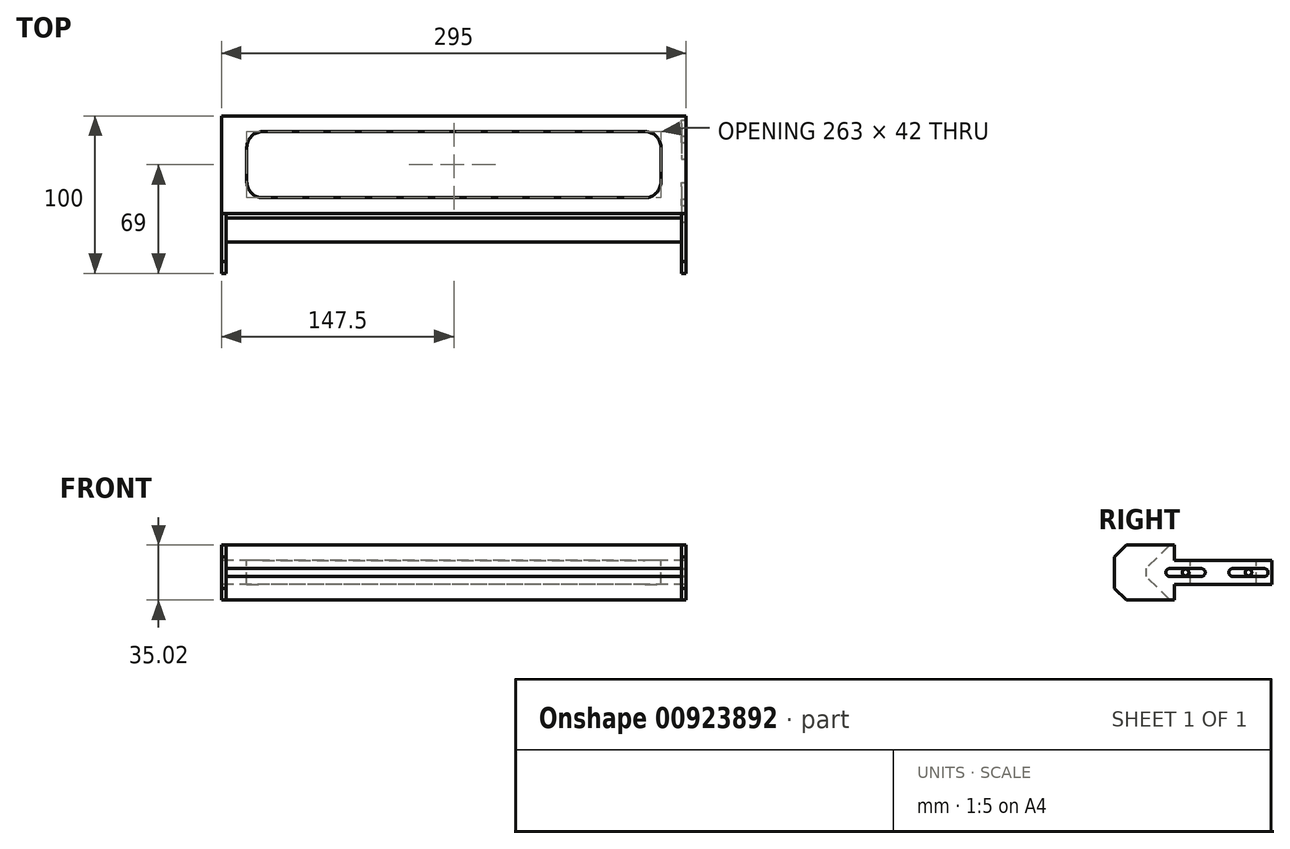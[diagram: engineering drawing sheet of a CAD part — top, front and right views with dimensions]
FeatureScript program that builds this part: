
annotation { "Feature Type Name" : "Feature", "Feature Type Description" : "" }
export const myFeature = defineFeature(function(context is Context, id is Id, definition is map)
    precondition{}
    {
        {
            var Q0;
            Q0=qCreatedBy(makeId("Top.planeOp"),FACE);
            var sketch = newSketch(context, id + "F0", { "sketchPlane" : qUnion([Q0])});
            skLineSegment(sketch, "E0.bottom", {"start": v(147.5, 50) * mm, "end": v(-147.5, 50) * mm});
            skLineSegment(sketch, "E0.top", {"start": v(147.5, -50) * mm, "end": v(144.5, -50) * mm});
            skLineSegment(sketch, "E0.left", {"start": v(147.5, 50) * mm, "end": v(147.5, -50) * mm});
            skLineSegment(sketch, "E0.right", {"start": v(-147.5, 50) * mm, "end": v(-147.5, -50) * mm});
            skPoint(sketch, "E0.middle", {"position": v(0, 0) * mm});
            skLineSegment(sketch, "E1", {"start": v(-144.5, -50) * mm, "end": v(-144.5, -30) * mm});
            skLineSegment(sketch, "E2", {"start": v(-144.5, -30) * mm, "end": v(144.5, -30) * mm});
            skLineSegment(sketch, "E3", {"start": v(144.5, -30) * mm, "end": v(144.5, -50) * mm});
            skLineSegment(sketch, "E4.trimOffspring", {"start": v(-144.5, -50) * mm, "end": v(-147.5, -50) * mm});
            skSolve(sketch);
        }
        {
            var Q0;
            Q0=qSketchRegion(id+"F0",true);
            extrude(context, id + "F1", {"entities" : qUnion([Q0]), "depth" : 17.5 * mm, "offsetDistance" : 25 * mm, "hasSecondDirection" : true, "secondDirectionOppositeDirection" : true, "secondDirectionDepth" : 17.5 * mm});
        }
        {
            var Q0;
            Q0=makeQuery(id+"F1.opExtrude","CAP_EDGE",EDGE,{"disambiguationData":[OSD([sQuery(id+"F0.wireOp",EDGE,"E2")])],"isStart":false});
            var Q1;
            Q1=makeQuery(id+"F1.opExtrude","CAP_EDGE",EDGE,{"disambiguationData":[OSD([sQuery(id+"F0.wireOp",EDGE,"E2")])],"isStart":true});
            chamfer(context, id + "F2", {"entities" : qUnion([Q0, Q1]), "width" : 15 * mm, "tangentPropagation" : true});
        }
        {
            var Q0;
            Q0=makeQuery(id+"F1.opExtrude","CAP_EDGE",EDGE,{"disambiguationData":[OSD([sQuery(id+"F0.wireOp",EDGE,"E0.top")])],"isStart":false});
            var Q1;
            Q1=makeQuery(id+"F1.opExtrude","CAP_EDGE",EDGE,{"disambiguationData":[OSD([sQuery(id+"F0.wireOp",EDGE,"E0.top")])],"isStart":true});
            var Q2;
            Q2=makeQuery(id+"F1.opExtrude","CAP_EDGE",EDGE,{"disambiguationData":[OSD([sQuery(id+"F0.wireOp",EDGE,"E4.trimOffspring")])],"isStart":false});
            var Q3;
            Q3=makeQuery(id+"F1.opExtrude","CAP_EDGE",EDGE,{"disambiguationData":[OSD([sQuery(id+"F0.wireOp",EDGE,"E4.trimOffspring")])],"isStart":true});
            chamfer(context, id + "F3", {"entities" : qUnion([Q0, Q1, Q2, Q3]), "width" : 7.5 * mm, "tangentPropagation" : true});
        }
        {
            var Q0;
            Q0=makeQuery(id+"F1.opExtrude","SWEPT_FACE",FACE,{"disambiguationData":[OSD([sQuery(id+"F0.wireOp",EDGE,"E0.left")])]});
            var sketch = newSketch(context, id + "F4", { "sketchPlane" : qUnion([Q0])});
            skLineSegment(sketch, "E5.bottom", {"start": v(45, 2.5) * mm, "end": v(25, 2.5) * mm});
            skLineSegment(sketch, "E5.top", {"start": v(45, -2.5) * mm, "end": v(25, -2.5) * mm});
            skLineSegment(sketch, "E5.left", {"start": v(47.5, 0) * mm, "end": v(47.5, 0) * mm});
            skLineSegment(sketch, "E5.right", {"start": v(22.5, 0) * mm, "end": v(22.5, 0) * mm});
            skLineSegment(sketch, "E6.bottom", {"start": v(5, 2.5) * mm, "end": v(-15, 2.5) * mm});
            skLineSegment(sketch, "E6.top", {"start": v(5, -2.5) * mm, "end": v(-15, -2.5) * mm});
            skLineSegment(sketch, "E6.left", {"start": v(7.5, 0) * mm, "end": v(7.5, 0) * mm});
            skLineSegment(sketch, "E6.right", {"start": v(-17.5, 0) * mm, "end": v(-17.5, 0) * mm});
            skPoint(sketch, "E7.visualSharp", {"position": v(-17.5, 2.5) * mm});
            skArc(sketch, "E7.filletArc", {"start": v(-15, 2.5) * mm, "mid": v(-16.77, 1.77) * mm, "end": v(-17.5, 0) * mm});
            skPoint(sketch, "E8.visualSharp", {"position": v(-17.5, -2.5) * mm});
            skArc(sketch, "E8.filletArc", {"start": v(-17.5, 0) * mm, "mid": v(-16.77, -1.77) * mm, "end": v(-15, -2.5) * mm});
            skPoint(sketch, "E9.visualSharp", {"position": v(7.5, 2.5) * mm});
            skArc(sketch, "E9.filletArc", {"start": v(7.5, 0) * mm, "mid": v(6.77, 1.77) * mm, "end": v(5, 2.5) * mm});
            skPoint(sketch, "E10.visualSharp", {"position": v(7.5, -2.5) * mm});
            skArc(sketch, "E10.filletArc", {"start": v(5, -2.5) * mm, "mid": v(6.77, -1.77) * mm, "end": v(7.5, 0) * mm});
            skPoint(sketch, "E11.visualSharp", {"position": v(22.5, 2.5) * mm});
            skArc(sketch, "E11.filletArc", {"start": v(25, 2.5) * mm, "mid": v(23.23, 1.77) * mm, "end": v(22.5, 0) * mm});
            skPoint(sketch, "E12.visualSharp", {"position": v(22.5, -2.5) * mm});
            skArc(sketch, "E12.filletArc", {"start": v(22.5, 0) * mm, "mid": v(23.23, -1.77) * mm, "end": v(25, -2.5) * mm});
            skPoint(sketch, "E13.visualSharp", {"position": v(47.5, 2.5) * mm});
            skArc(sketch, "E13.filletArc", {"start": v(47.5, 0) * mm, "mid": v(46.77, 1.77) * mm, "end": v(45, 2.5) * mm});
            skPoint(sketch, "E14.visualSharp", {"position": v(47.5, -2.5) * mm});
            skArc(sketch, "E14.filletArc", {"start": v(45, -2.5) * mm, "mid": v(46.77, -1.77) * mm, "end": v(47.5, 0) * mm});
            skCircle(sketch, "E15", {"center": v(-5, 0) * mm, "radius": 2.1 * mm});
            skCircle(sketch, "E16", {"center": v(35, 0) * mm, "radius": 2.1 * mm});
            skPoint(sketch, "E16.centerSnap0", {"position": v(35, -2.5) * mm});
            skLineSegment(sketch, "E17", {"start": v(-50, 0) * mm, "end": v(50, 0) * mm, "construction": true});
            skSolve(sketch);
        }
        {
            var Q0;
            Q0=makeQuery(id+"F1.opExtrude","CAP_FACE",FACE,{"disambiguationData":[OSD([sQuery(id+"F0.wireOp",EDGE,"E0.bottom"),sQuery(id+"F0.wireOp",EDGE,"E0.top"),sQuery(id+"F0.wireOp",EDGE,"E0.left"),sQuery(id+"F0.wireOp",EDGE,"E0.right"),sQuery(id+"F0.wireOp",EDGE,"E1"),sQuery(id+"F0.wireOp",EDGE,"E2"),sQuery(id+"F0.wireOp",EDGE,"E3"),sQuery(id+"F0.wireOp",EDGE,"E4.trimOffspring")])],"isStart":false});
            var sketch = newSketch(context, id + "F5", { "sketchPlane" : qUnion([Q0])});
            skLineSegment(sketch, "E18.bottom", {"start": v(-147.5, 50) * mm, "end": v(-144.5, 50) * mm});
            skLineSegment(sketch, "E18.top", {"start": v(-147.5, -42.5) * mm, "end": v(-144.5, -42.5) * mm});
            skLineSegment(sketch, "E18.left", {"start": v(-147.5, 50) * mm, "end": v(-147.5, -42.5) * mm});
            skLineSegment(sketch, "E18.right", {"start": v(-144.5, 50) * mm, "end": v(-144.5, -42.5) * mm});
            skLineSegment(sketch, "E19.bottom", {"start": v(147.5, 50) * mm, "end": v(144.5, 50) * mm});
            skLineSegment(sketch, "E19.top", {"start": v(147.5, -42.5) * mm, "end": v(144.5, -42.5) * mm});
            skLineSegment(sketch, "E19.left", {"start": v(147.5, 50) * mm, "end": v(147.5, -42.5) * mm});
            skLineSegment(sketch, "E19.right", {"start": v(144.5, 50) * mm, "end": v(144.5, -42.5) * mm});
            skSolve(sketch);
        }
        {
            var Q0;
            Q0=qSketchRegion(id+"F5",true);
            extrude(context, id + "F6", {"entities" : qUnion([Q0]), "operationType" : NewBodyOperationType.ADD, "depth" : 0.01 * mm, "offsetDistance" : 25 * mm});
        }
        {
            var Q0;
            Q0=makeQuery(id+"F1.opExtrude","CAP_FACE",FACE,{"disambiguationData":[OSD([sQuery(id+"F0.wireOp",EDGE,"E0.bottom"),sQuery(id+"F0.wireOp",EDGE,"E0.top"),sQuery(id+"F0.wireOp",EDGE,"E0.left"),sQuery(id+"F0.wireOp",EDGE,"E0.right"),sQuery(id+"F0.wireOp",EDGE,"E1"),sQuery(id+"F0.wireOp",EDGE,"E2"),sQuery(id+"F0.wireOp",EDGE,"E3"),sQuery(id+"F0.wireOp",EDGE,"E4.trimOffspring")])],"isStart":true});
            var sketch = newSketch(context, id + "F7", { "sketchPlane" : qUnion([Q0])});
            skLineSegment(sketch, "E20.bottom", {"start": v(-147.5, -50) * mm, "end": v(-144.5, -50) * mm});
            skLineSegment(sketch, "E20.top", {"start": v(-147.5, 42.5) * mm, "end": v(-144.5, 42.5) * mm});
            skLineSegment(sketch, "E20.left", {"start": v(-147.5, -50) * mm, "end": v(-147.5, 42.5) * mm});
            skLineSegment(sketch, "E20.right", {"start": v(-144.5, -50) * mm, "end": v(-144.5, 42.5) * mm});
            skLineSegment(sketch, "E21.bottom", {"start": v(147.5, -50) * mm, "end": v(144.5, -50) * mm});
            skLineSegment(sketch, "E21.top", {"start": v(147.5, 42.5) * mm, "end": v(144.5, 42.5) * mm});
            skLineSegment(sketch, "E21.left", {"start": v(147.5, -50) * mm, "end": v(147.5, 42.5) * mm});
            skLineSegment(sketch, "E21.right", {"start": v(144.5, -50) * mm, "end": v(144.5, 42.5) * mm});
            skSolve(sketch);
        }
        {
            var Q0;
            Q0=qSketchRegion(id+"F7",true);
            extrude(context, id + "F8", {"entities" : qUnion([Q0]), "operationType" : NewBodyOperationType.ADD, "depth" : 0.01 * mm, "offsetDistance" : 25 * mm});
        }
        {
            var Q0;
            Q0=makeQuery(id+"F4.imprint","IMPRINT",FACE,{"disambiguationData":[TD([[makeQuery(id+"F4.imprint","IMPRINT",EDGE,{"derivedFrom":sQuery(id+"F4.wireOp",EDGE,"E5.bottom")}),1.0]])]});
            var Q1;
            Q1=makeQuery(id+"F4.imprint","IMPRINT",FACE,{"disambiguationData":[TD([[makeQuery(id+"F4.imprint","IMPRINT",EDGE,{"derivedFrom":sQuery(id+"F4.wireOp",EDGE,"E6.bottom")}),1.0]])]});
            extrude(context, id + "F9", {"entities" : qUnion([Q0, Q1]), "operationType" : NewBodyOperationType.REMOVE, "oppositeDirection" : true, "depth" : 3 * mm, "offsetDistance" : 25 * mm});
        }
        {
            var Q0;
            Q0=makeQuery(id+"F1.opExtrude","CAP_FACE",FACE,{"disambiguationData":[OSD([sQuery(id+"F0.wireOp",EDGE,"E0.bottom"),sQuery(id+"F0.wireOp",EDGE,"E0.top"),sQuery(id+"F0.wireOp",EDGE,"E0.left"),sQuery(id+"F0.wireOp",EDGE,"E0.right"),sQuery(id+"F0.wireOp",EDGE,"E1"),sQuery(id+"F0.wireOp",EDGE,"E2"),sQuery(id+"F0.wireOp",EDGE,"E3"),sQuery(id+"F0.wireOp",EDGE,"E4.trimOffspring")])],"isStart":false});
            var sketch = newSketch(context, id + "F10", { "sketchPlane" : qUnion([Q0])});
            skLineSegment(sketch, "E22.bottom", {"start": v(-141.5, 50) * mm, "end": v(141.5, 50) * mm});
            skLineSegment(sketch, "E22.top", {"start": v(-131.5, -12) * mm, "end": v(131.5, -12) * mm});
            skLineSegment(sketch, "E22.left", {"start": v(-141.5, 50) * mm, "end": v(-141.5, -2) * mm});
            skLineSegment(sketch, "E22.right", {"start": v(141.5, 50) * mm, "end": v(141.5, -2) * mm});
            skPoint(sketch, "E23.visualSharp", {"position": v(-141.5, -12) * mm});
            skArc(sketch, "E23.filletArc", {"start": v(-141.5, -2) * mm, "mid": v(-138.57, -9.07) * mm, "end": v(-131.5, -12) * mm});
            skPoint(sketch, "E24.visualSharp", {"position": v(141.5, -12) * mm});
            skArc(sketch, "E24.filletArc", {"start": v(131.5, -12) * mm, "mid": v(138.57, -9.07) * mm, "end": v(141.5, -2) * mm});
            skSolve(sketch);
        }
        {
            var Q0;
            Q0=makeQuery(id+"F10.imprint","IMPRINT",FACE,{"disambiguationData":[TD([[makeQuery(id+"F10.imprint","IMPRINT",EDGE,{"derivedFrom":sQuery(id+"F10.wireOp",EDGE,"E22.bottom")}),1.0]])]});
            extrude(context, id + "F11", {"entities" : qUnion([Q0]), "operationType" : NewBodyOperationType.REMOVE, "oppositeDirection" : true, "depth" : 10 * mm, "offsetDistance" : 25 * mm});
        }
        {
            var Q0;
            Q0=makeQuery(id+"F1.opExtrude","CAP_FACE",FACE,{"disambiguationData":[OSD([sQuery(id+"F0.wireOp",EDGE,"E0.bottom"),sQuery(id+"F0.wireOp",EDGE,"E0.top"),sQuery(id+"F0.wireOp",EDGE,"E0.left"),sQuery(id+"F0.wireOp",EDGE,"E0.right"),sQuery(id+"F0.wireOp",EDGE,"E1"),sQuery(id+"F0.wireOp",EDGE,"E2"),sQuery(id+"F0.wireOp",EDGE,"E3"),sQuery(id+"F0.wireOp",EDGE,"E4.trimOffspring")])],"isStart":true});
            var sketch = newSketch(context, id + "F12", { "sketchPlane" : qUnion([Q0])});
            skLineSegment(sketch, "E25.0.0", {"start": v(141.5, 2) * mm, "end": v(141.5, -50) * mm});
            skLineSegment(sketch, "E25.0.1", {"start": v(141.5, -50) * mm, "end": v(-141.5, -50) * mm});
            skLineSegment(sketch, "E25.0.2", {"start": v(-141.5, -50) * mm, "end": v(-141.5, 2) * mm});
            skArc(sketch, "E25.0.3", {"start": v(-141.5, 2) * mm, "mid": v(-138.57, 9.07) * mm, "end": v(-131.5, 12) * mm});
            skLineSegment(sketch, "E25.0.4", {"start": v(-131.5, 12) * mm, "end": v(131.5, 12) * mm});
            skArc(sketch, "E25.0.5", {"start": v(131.5, 12) * mm, "mid": v(138.57, 9.07) * mm, "end": v(141.5, 2) * mm});
            skSolve(sketch);
        }
        {
            var Q0;
            Q0=qSketchRegion(id+"F12",true);
            extrude(context, id + "F13", {"entities" : qUnion([Q0]), "operationType" : NewBodyOperationType.REMOVE, "oppositeDirection" : true, "depth" : 10 * mm, "offsetDistance" : 25 * mm});
        }
        {
            var Q0;
            Q0=makeQuery(id+"F11.boolean.opBoolean","COPY",FACE,{"derivedFrom":makeQuery(id+"F11.opExtrude","CAP_FACE",FACE,{"disambiguationData":[OSD([sQuery(id+"F10.wireOp",EDGE,"E22.bottom"),sQuery(id+"F10.wireOp",EDGE,"E22.top"),sQuery(id+"F10.wireOp",EDGE,"E22.left"),sQuery(id+"F10.wireOp",EDGE,"E22.right"),sQuery(id+"F10.wireOp",EDGE,"E23.filletArc"),sQuery(id+"F10.wireOp",EDGE,"E24.filletArc")])],"isStart":false})});
            var sketch = newSketch(context, id + "F14", { "sketchPlane" : qUnion([Q0])});
            skLineSegment(sketch, "E26.bottom", {"start": v(-121.5, 40) * mm, "end": v(121.5, 40) * mm});
            skLineSegment(sketch, "E26.top", {"start": v(-121.5, -2) * mm, "end": v(121.5, -2) * mm});
            skLineSegment(sketch, "E26.left", {"start": v(-131.5, 30) * mm, "end": v(-131.5, 8) * mm});
            skLineSegment(sketch, "E26.right", {"start": v(131.5, 30) * mm, "end": v(131.5, 8) * mm});
            skPoint(sketch, "E27.visualSharp", {"position": v(-131.5, 40) * mm});
            skArc(sketch, "E27.filletArc", {"start": v(-121.5, 40) * mm, "mid": v(-128.57, 37.07) * mm, "end": v(-131.5, 30) * mm});
            skPoint(sketch, "E28.visualSharp", {"position": v(-131.5, -2) * mm});
            skArc(sketch, "E28.filletArc", {"start": v(-131.5, 8) * mm, "mid": v(-128.57, 0.93) * mm, "end": v(-121.5, -2) * mm});
            skPoint(sketch, "E29.visualSharp", {"position": v(131.5, 40) * mm});
            skArc(sketch, "E29.filletArc", {"start": v(131.5, 30) * mm, "mid": v(128.57, 37.07) * mm, "end": v(121.5, 40) * mm});
            skPoint(sketch, "E30.visualSharp", {"position": v(131.5, -2) * mm});
            skArc(sketch, "E30.filletArc", {"start": v(121.5, -2) * mm, "mid": v(128.57, 0.93) * mm, "end": v(131.5, 8) * mm});
            skSolve(sketch);
        }
        {
            var Q0;
            Q0=makeQuery(id+"F14.imprint","IMPRINT",FACE,{"disambiguationData":[TD([[makeQuery(id+"F14.imprint","IMPRINT",EDGE,{"derivedFrom":sQuery(id+"F14.wireOp",EDGE,"E26.bottom")}),-1.0]])]});
            extrude(context, id + "F15", {"entities" : qUnion([Q0]), "operationType" : NewBodyOperationType.REMOVE, "oppositeDirection" : true, "depth" : 25 * mm, "offsetDistance" : 25 * mm});
        }
        {
            var Q0;
            Q0=makeQuery(id+"F1.opExtrude","CAP_FACE",FACE,{"disambiguationData":[OSD([sQuery(id+"F0.wireOp",EDGE,"E0.bottom"),sQuery(id+"F0.wireOp",EDGE,"E0.top"),sQuery(id+"F0.wireOp",EDGE,"E0.left"),sQuery(id+"F0.wireOp",EDGE,"E0.right"),sQuery(id+"F0.wireOp",EDGE,"E1"),sQuery(id+"F0.wireOp",EDGE,"E2"),sQuery(id+"F0.wireOp",EDGE,"E3"),sQuery(id+"F0.wireOp",EDGE,"E4.trimOffspring")])],"isStart":false});
            var sketch = newSketch(context, id + "F16", { "sketchPlane" : qUnion([Q0])});
            skLineSegment(sketch, "E31.bottom", {"start": v(-147.5, 50) * mm, "end": v(147.5, 50) * mm});
            skLineSegment(sketch, "E31.top", {"start": v(-147.5, -12) * mm, "end": v(147.5, -12) * mm});
            skLineSegment(sketch, "E31.left", {"start": v(-147.5, 50) * mm, "end": v(-147.5, -12) * mm});
            skLineSegment(sketch, "E31.right", {"start": v(147.5, 50) * mm, "end": v(147.5, -12) * mm});
            skSolve(sketch);
        }
        {
            var Q0;
            Q0 = qSketchRegion(id + "F16", true);
            var Q1;
            Q1=makeQuery(id+"F11.boolean.opBoolean","COPY",FACE,{"derivedFrom":makeQuery(id+"F11.opExtrude","CAP_FACE",FACE,{"disambiguationData":[OSD([sQuery(id+"F10.wireOp",EDGE,"E22.bottom"),sQuery(id+"F10.wireOp",EDGE,"E22.top"),sQuery(id+"F10.wireOp",EDGE,"E22.left"),sQuery(id+"F10.wireOp",EDGE,"E22.right"),sQuery(id+"F10.wireOp",EDGE,"E23.filletArc"),sQuery(id+"F10.wireOp",EDGE,"E24.filletArc")])],"isStart":false})});
            extrude(context, id + "F17", {"entities" : qUnion([Q0]), "operationType" : NewBodyOperationType.REMOVE, "endBound" : BoundingType.UP_TO_SURFACE, "oppositeDirection" : true, "depth" : 25 * mm, "endBoundEntityFace" : qUnion([Q1]), "offsetDistance" : 25 * mm, "hasSecondDirection" : true, "secondDirectionOppositeDirection" : false, "secondDirectionDepth" : 25 * mm});
        }
        {
            var Q0;
            Q0=makeQuery(id+"F1.opExtrude","CAP_FACE",FACE,{"disambiguationData":[OSD([sQuery(id+"F0.wireOp",EDGE,"E0.bottom"),sQuery(id+"F0.wireOp",EDGE,"E0.top"),sQuery(id+"F0.wireOp",EDGE,"E0.left"),sQuery(id+"F0.wireOp",EDGE,"E0.right"),sQuery(id+"F0.wireOp",EDGE,"E1"),sQuery(id+"F0.wireOp",EDGE,"E2"),sQuery(id+"F0.wireOp",EDGE,"E3"),sQuery(id+"F0.wireOp",EDGE,"E4.trimOffspring")])],"isStart":true});
            var sketch = newSketch(context, id + "F18", { "sketchPlane" : qUnion([Q0])});
            skLineSegment(sketch, "E32.bottom", {"start": v(-147.5, -50) * mm, "end": v(147.5, -50) * mm});
            skLineSegment(sketch, "E32.top", {"start": v(-147.5, 12) * mm, "end": v(147.5, 12) * mm});
            skLineSegment(sketch, "E32.left", {"start": v(-147.5, -50) * mm, "end": v(-147.5, 12) * mm});
            skLineSegment(sketch, "E32.right", {"start": v(147.5, -50) * mm, "end": v(147.5, 12) * mm});
            skSolve(sketch);
        }
        {
            var Q0;
            Q0 = qSketchRegion(id + "F18", true);
            var Q1;
            Q1=makeQuery(id+"F13.boolean.opBoolean","COPY",FACE,{"derivedFrom":makeQuery(id+"F13.opExtrude","CAP_FACE",FACE,{"disambiguationData":[OSD([sQuery(id+"F12.wireOp",EDGE,"E25.0.0"),sQuery(id+"F12.wireOp",EDGE,"E25.0.1"),sQuery(id+"F12.wireOp",EDGE,"E25.0.2"),sQuery(id+"F12.wireOp",EDGE,"E25.0.3"),sQuery(id+"F12.wireOp",EDGE,"E25.0.4"),sQuery(id+"F12.wireOp",EDGE,"E25.0.5")])],"isStart":false})});
            extrude(context, id + "F19", {"entities" : qUnion([Q0]), "operationType" : NewBodyOperationType.REMOVE, "endBound" : BoundingType.UP_TO_SURFACE, "oppositeDirection" : true, "depth" : 25 * mm, "endBoundEntityFace" : qUnion([Q1]), "offsetDistance" : 25 * mm, "hasSecondDirection" : true, "secondDirectionOppositeDirection" : false, "secondDirectionDepth" : 25 * mm});
        }
    });
